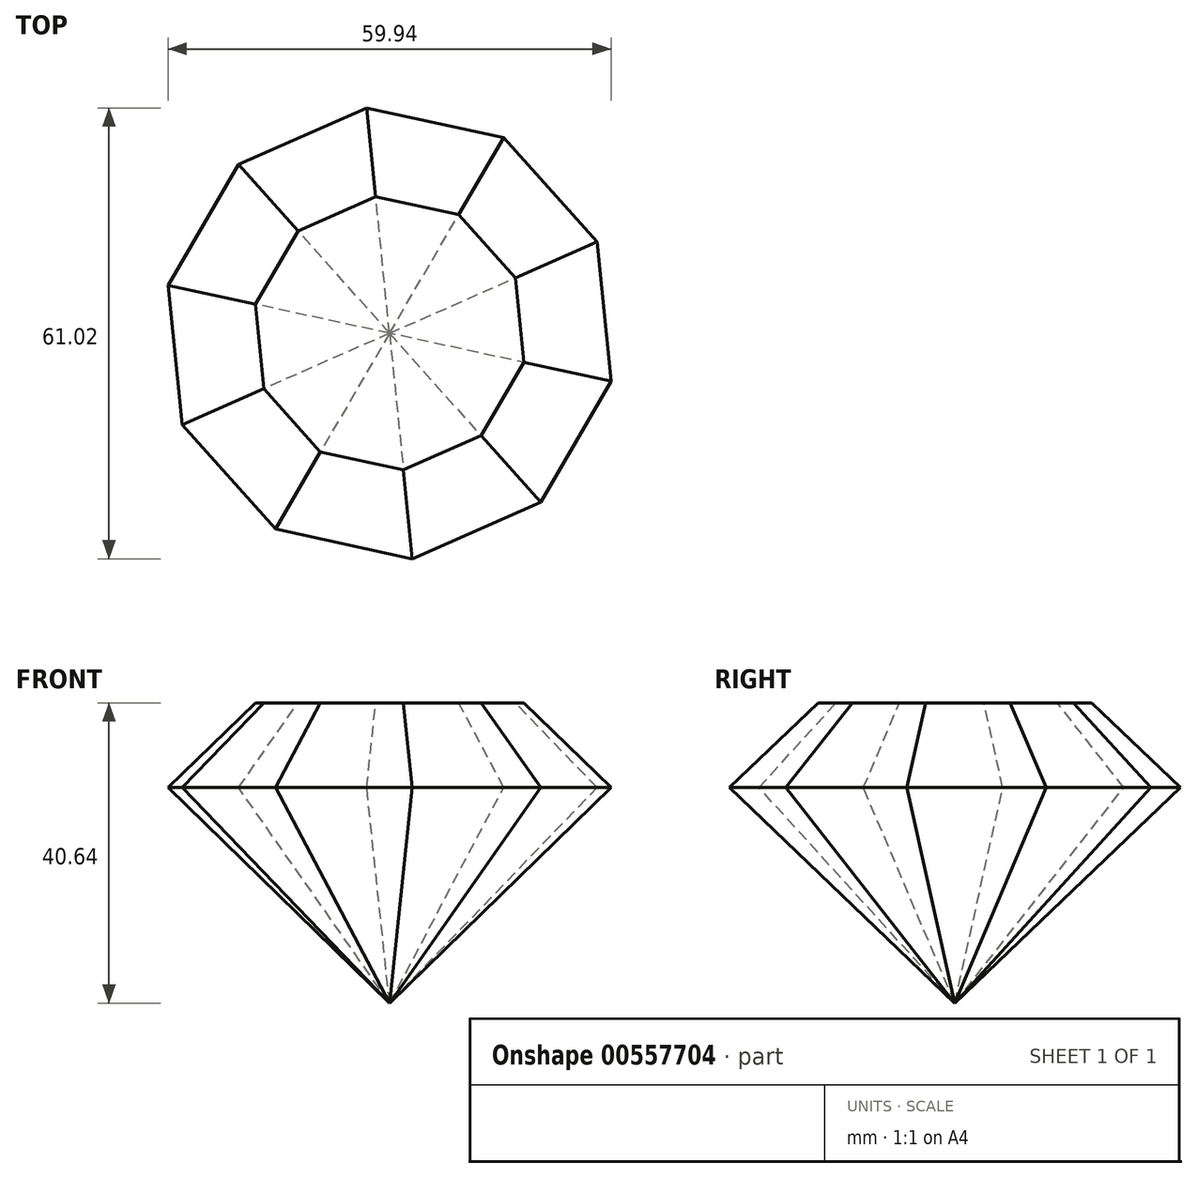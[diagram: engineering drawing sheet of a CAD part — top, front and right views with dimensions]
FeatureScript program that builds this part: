
annotation { "Feature Type Name" : "Feature", "Feature Type Description" : "" }
export const myFeature = defineFeature(function(context is Context, id is Id, definition is map)
    precondition{}
    {
        {
            var Q0;
            Q0=qCreatedBy(makeId("Top.planeOp"),FACE);
            var sketch = newSketch(context, id + "F0", { "sketchPlane" : qUnion([Q0])});
            skCircle(sketch, "E0.cCircle", {"center": v(0, 0) * mm, "radius": 31.95 * mm, "construction": true});
            skLineSegment(sketch, "E0.0", {"start": v(16.08, 27.61) * mm, "end": v(29.24, 12.88) * mm});
            skLineSegment(sketch, "E0.1", {"start": v(29.24, 12.88) * mm, "end": v(31.23, -6.76) * mm});
            skLineSegment(sketch, "E0.2", {"start": v(31.23, -6.76) * mm, "end": v(21.29, -23.83) * mm});
            skLineSegment(sketch, "E0.3", {"start": v(21.29, -23.83) * mm, "end": v(3.22, -31.8) * mm});
            skLineSegment(sketch, "E0.4", {"start": v(3.22, -31.8) * mm, "end": v(-16.08, -27.61) * mm});
            skLineSegment(sketch, "E0.5", {"start": v(-16.08, -27.61) * mm, "end": v(-29.24, -12.88) * mm});
            skLineSegment(sketch, "E0.6", {"start": v(-29.24, -12.88) * mm, "end": v(-31.23, 6.76) * mm});
            skLineSegment(sketch, "E0.7", {"start": v(-31.23, 6.76) * mm, "end": v(-21.29, 23.83) * mm});
            skLineSegment(sketch, "E0.8", {"start": v(-21.29, 23.83) * mm, "end": v(-3.22, 31.8) * mm});
            skLineSegment(sketch, "E0.9", {"start": v(-3.22, 31.8) * mm, "end": v(16.08, 27.61) * mm});
            skSolve(sketch);
        }
        {
            var Q0;
            Q0=makeQuery(id+"F0.imprint","IMPRINT",FACE,{"disambiguationData":[TD([[makeQuery(id+"F0.imprint","IMPRINT",EDGE,{"derivedFrom":sQuery(id+"F0.wireOp",EDGE,"E0.0")}),-1.0]])]});
            extrude(context, id + "F1", {"entities" : qUnion([Q0]), "depth" : 40.64 * mm, "offsetDistance" : 25.4 * mm});
        }
        {
            var Q0;
            Q0=makeQuery(id+"F1.opExtrude","CAP_EDGE",EDGE,{"disambiguationData":[OSD([sQuery(id+"F0.wireOp",EDGE,"E0.3")])],"isStart":false});
            var Q1;
            Q1=makeQuery(id+"F1.opExtrude","CAP_EDGE",EDGE,{"disambiguationData":[OSD([sQuery(id+"F0.wireOp",EDGE,"E0.2")])],"isStart":false});
            var Q2;
            Q2=makeQuery(id+"F1.opExtrude","CAP_EDGE",EDGE,{"disambiguationData":[OSD([sQuery(id+"F0.wireOp",EDGE,"E0.1")])],"isStart":false});
            var Q3;
            Q3=makeQuery(id+"F1.opExtrude","CAP_EDGE",EDGE,{"disambiguationData":[OSD([sQuery(id+"F0.wireOp",EDGE,"E0.0")])],"isStart":false});
            var Q4;
            Q4=makeQuery(id+"F1.opExtrude","CAP_EDGE",EDGE,{"disambiguationData":[OSD([sQuery(id+"F0.wireOp",EDGE,"E0.9")])],"isStart":false});
            var Q5;
            Q5=makeQuery(id+"F1.opExtrude","CAP_EDGE",EDGE,{"disambiguationData":[OSD([sQuery(id+"F0.wireOp",EDGE,"E0.8")])],"isStart":false});
            var Q6;
            Q6=makeQuery(id+"F1.opExtrude","CAP_EDGE",EDGE,{"disambiguationData":[OSD([sQuery(id+"F0.wireOp",EDGE,"E0.7")])],"isStart":false});
            var Q7;
            Q7=makeQuery(id+"F1.opExtrude","CAP_EDGE",EDGE,{"disambiguationData":[OSD([sQuery(id+"F0.wireOp",EDGE,"E0.6")])],"isStart":false});
            var Q8;
            Q8=makeQuery(id+"F1.opExtrude","CAP_EDGE",EDGE,{"disambiguationData":[OSD([sQuery(id+"F0.wireOp",EDGE,"E0.5")])],"isStart":false});
            var Q9;
            Q9=makeQuery(id+"F1.opExtrude","CAP_EDGE",EDGE,{"disambiguationData":[OSD([sQuery(id+"F0.wireOp",EDGE,"E0.4")])],"isStart":false});
            chamfer(context, id + "F2", {"entities" : qUnion([Q0, Q1, Q2, Q3, Q4, Q5, Q6, Q7, Q8, Q9]), "width" : 12.7 * mm, "tangentPropagation" : true});
        }
        {
            var Q0;
            Q0=makeQuery(id+"F1.opExtrude","CAP_EDGE",EDGE,{"disambiguationData":[OSD([sQuery(id+"F0.wireOp",EDGE,"E0.4")])],"isStart":true});
            var Q1;
            Q1=makeQuery(id+"F1.opExtrude","CAP_FACE",FACE,{"disambiguationData":[OSD([sQuery(id+"F0.wireOp",EDGE,"E0.0"),sQuery(id+"F0.wireOp",EDGE,"E0.1"),sQuery(id+"F0.wireOp",EDGE,"E0.2"),sQuery(id+"F0.wireOp",EDGE,"E0.3"),sQuery(id+"F0.wireOp",EDGE,"E0.4"),sQuery(id+"F0.wireOp",EDGE,"E0.5"),sQuery(id+"F0.wireOp",EDGE,"E0.6"),sQuery(id+"F0.wireOp",EDGE,"E0.7"),sQuery(id+"F0.wireOp",EDGE,"E0.8"),sQuery(id+"F0.wireOp",EDGE,"E0.9")])],"isStart":true});
            chamfer(context, id + "F3", {"entities" : qUnion([Q0, Q1]), "width" : 30.4 * mm, "tangentPropagation" : true});
        }
    });
